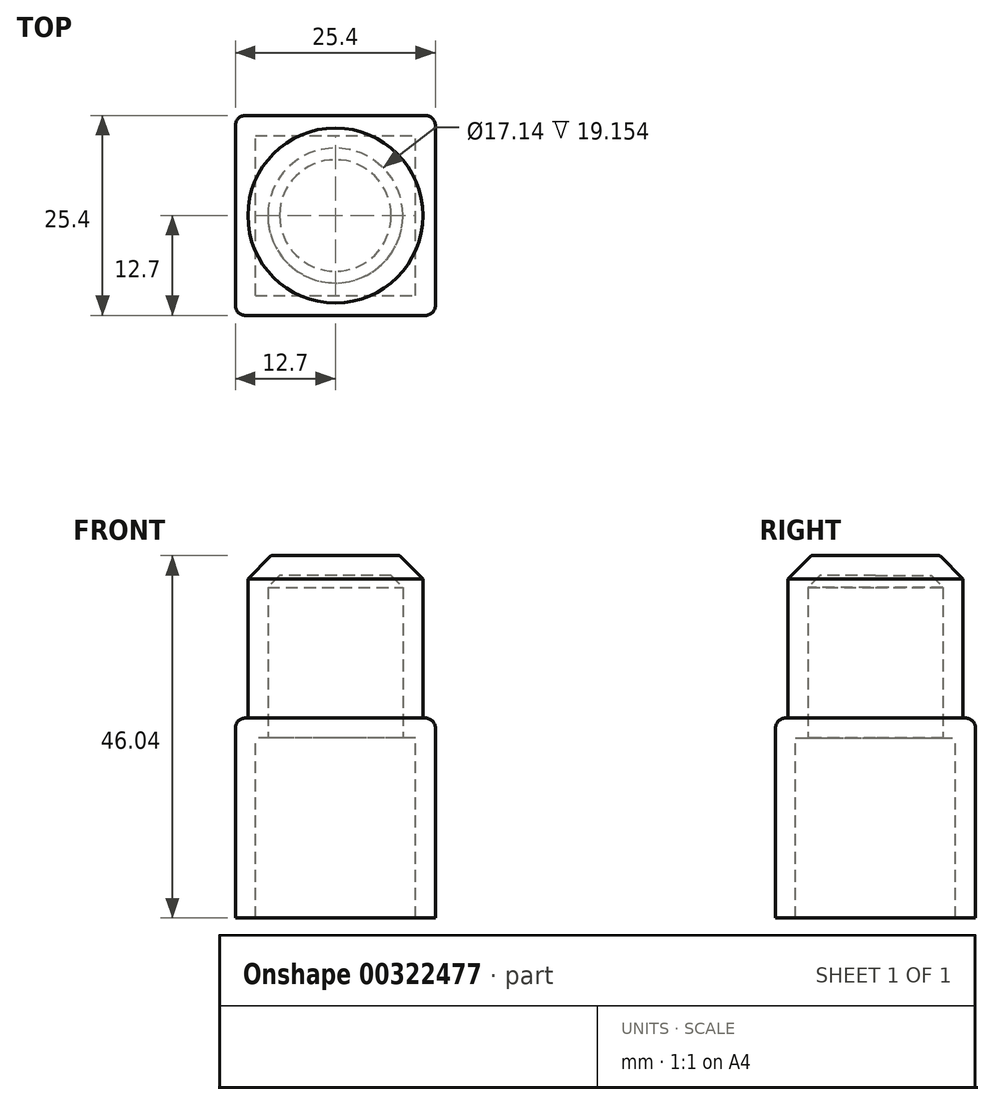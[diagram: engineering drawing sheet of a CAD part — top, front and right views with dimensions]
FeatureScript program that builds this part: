
annotation { "Feature Type Name" : "Feature", "Feature Type Description" : "" }
export const myFeature = defineFeature(function(context is Context, id is Id, definition is map)
    precondition{}
    {
        {
            var Q0;
            Q0=qCreatedBy(makeId("Front.planeOp"),FACE);
            var sketch = newSketch(context, id + "F0", { "sketchPlane" : qUnion([Q0])});
            skLineSegment(sketch, "E0.bottom", {"start": v(-12.7, 12.7) * mm, "end": v(12.7, 12.7) * mm});
            skLineSegment(sketch, "E0.top", {"start": v(-12.7, -12.7) * mm, "end": v(12.7, -12.7) * mm});
            skLineSegment(sketch, "E0.left", {"start": v(-12.7, 12.7) * mm, "end": v(-12.7, -12.7) * mm});
            skLineSegment(sketch, "E0.right", {"start": v(12.7, 12.7) * mm, "end": v(12.7, -12.7) * mm});
            skPoint(sketch, "E0.middle", {"position": v(0, 0) * mm});
            skSolve(sketch);
        }
        {
            var Q0;
            Q0 = qSketchRegion(id + "F0", true);
            extrude(context, id + "F1", {"entities" : qUnion([Q0]), "depth" : 25.4 * mm, "symmetric" : true});
        }
        {
            var Q0;
            Q0=makeQuery(id+"F1.opExtrude","SWEPT_FACE",FACE,{"disambiguationData":[OSD([sQuery(id+"F0.wireOp",EDGE,"E0.bottom")])]});
            var sketch = newSketch(context, id + "F2", { "sketchPlane" : qUnion([Q0])});
            skCircle(sketch, "E1", {"center": v(0, 0) * mm, "radius": 11.11 * mm});
            skSolve(sketch);
        }
        {
            var Q0;
            Q0 = qSketchRegion(id + "F2", true);
            extrude(context, id + "F3", {"entities" : qUnion([Q0]), "operationType" : NewBodyOperationType.ADD, "depth" : 20.64 * mm});
        }
        {
            var Q0;
            Q0=makeQuery(id+"F3.opExtrude","CAP_EDGE",EDGE,{"disambiguationData":[OSD([sQuery(id+"F2.wireOp",EDGE,"E1")])],"isStart":false});
            chamfer(context, id + "F4", {"entities" : qUnion([Q0]), "width" : 2.97 * mm, "tangentPropagation" : true});
        }
        {
            var Q0;
            {var subQ0=sQuery(id+"F2.wireOp",EDGE,"E1");Q0=makeQuery(id+"F4.opChamfer","BLEND_EDGE",EDGE,{"blendedFrom":[makeQuery(id+"F3.opExtrude","CAP_EDGE",EDGE,{"disambiguationData":[OSD([subQ0])],"isStart":false}),makeQuery(id+"F3.opExtrude","CAP_FACE",FACE,{"disambiguationData":[OSD([subQ0])],"isStart":false})],"blendedInto":[makeQuery(id+"F3.opExtrude","CAP_FACE",FACE,{"disambiguationData":[OSD([subQ0])],"isStart":false})]});}
            fillet(context, id + "F5", {"entities" : qUnion([Q0]), "radius" : 0.25 * mm, "tangentPropagation" : true, "allowEdgeOverflow" : false});
        }
        {
            var Q0;
            Q0=makeQuery(id+"F1.opExtrude","CAP_EDGE",EDGE,{"disambiguationData":[OSD([sQuery(id+"F0.wireOp",EDGE,"E0.bottom")])],"isStart":false});
            fillet(context, id + "F6", {"entities" : qUnion([Q0]), "radius" : 1.27 * mm, "tangentPropagation" : true, "allowEdgeOverflow" : false});
        }
        {
            var Q0;
            Q0=makeQuery(id+"F1.opExtrude","SWEPT_EDGE",EDGE,{"disambiguationData":[OSD([sQuery(id+"F0.wireOp",EDGE,"E0.bottom"),sQuery(id+"F0.wireOp",EDGE,"E0.right")])]});
            fillet(context, id + "F7", {"entities" : qUnion([Q0]), "radius" : 1.27 * mm, "tangentPropagation" : true, "allowEdgeOverflow" : false});
        }
        {
            var Q0;
            Q0=makeQuery(id+"F1.opExtrude","SWEPT_EDGE",EDGE,{"disambiguationData":[OSD([sQuery(id+"F0.wireOp",EDGE,"E0.bottom"),sQuery(id+"F0.wireOp",EDGE,"E0.left")])]});
            fillet(context, id + "F8", {"entities" : qUnion([Q0]), "radius" : 1.27 * mm, "tangentPropagation" : true, "allowEdgeOverflow" : false});
        }
        {
            var Q0;
            Q0=makeQuery(id+"F1.opExtrude","CAP_EDGE",EDGE,{"disambiguationData":[OSD([sQuery(id+"F0.wireOp",EDGE,"E0.bottom")])],"isStart":true});
            fillet(context, id + "F9", {"entities" : qUnion([Q0]), "radius" : 1.27 * mm, "tangentPropagation" : true, "allowEdgeOverflow" : false});
        }
        {
            var Q0;
            Q0=makeQuery(id+"F1.opExtrude","SWEPT_FACE",FACE,{"disambiguationData":[OSD([sQuery(id+"F0.wireOp",EDGE,"E0.top")])]});
            shell(context, id + "F10", {"entities" : qUnion([Q0]), "thickness" : 2.54 * mm});
        }
    });
